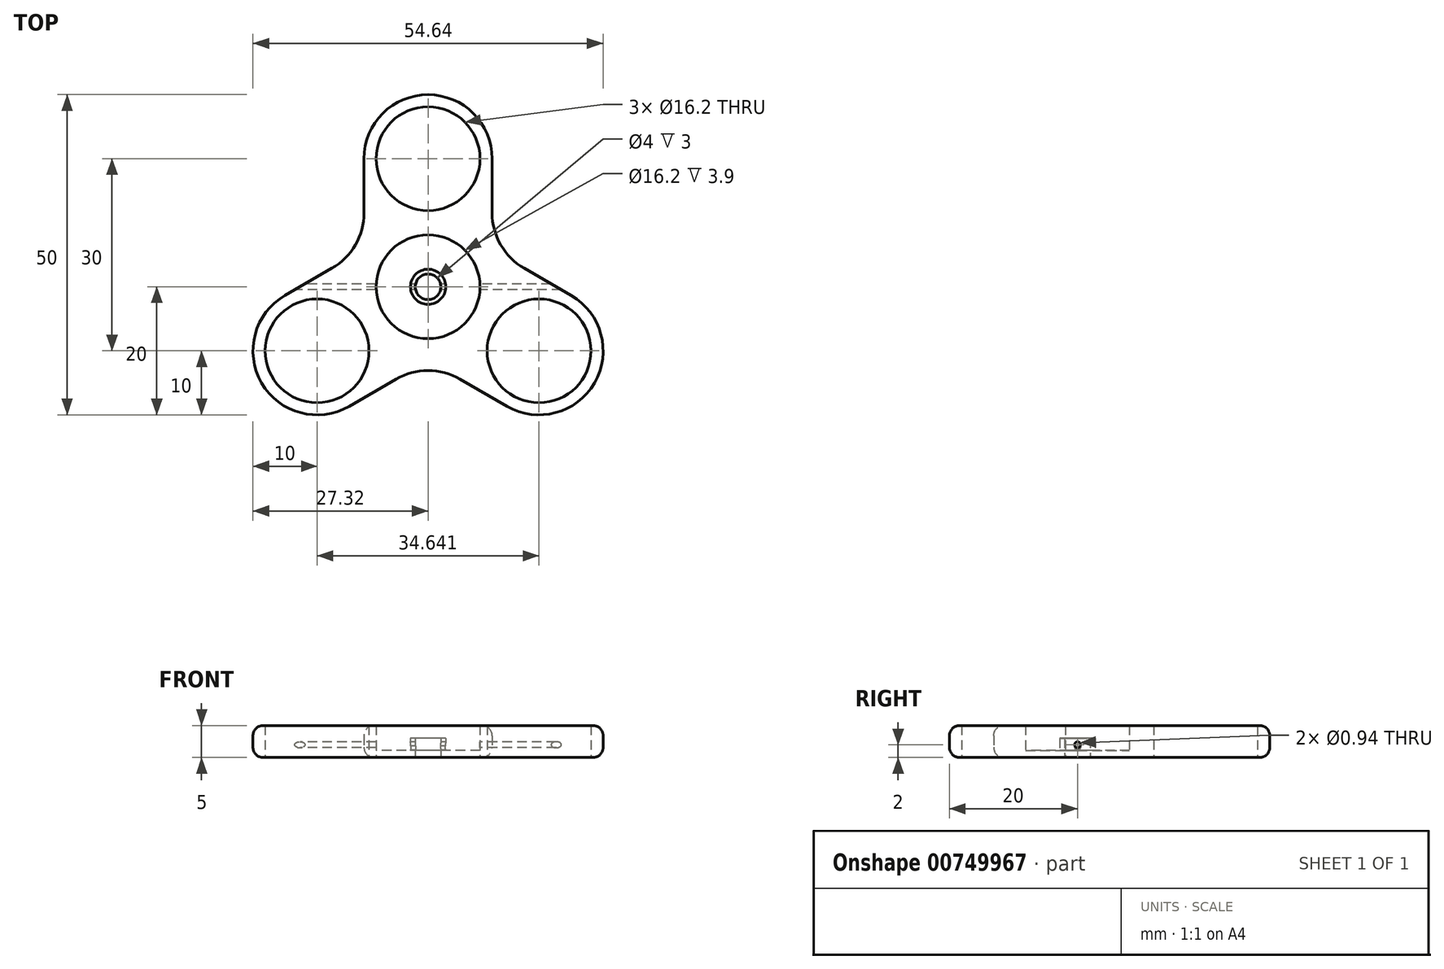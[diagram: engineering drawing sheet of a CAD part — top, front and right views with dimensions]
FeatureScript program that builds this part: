
annotation { "Feature Type Name" : "Feature", "Feature Type Description" : "" }
export const myFeature = defineFeature(function(context is Context, id is Id, definition is map)
    precondition{}
    {
        {
            var Q0;
            Q0=qCreatedBy(makeId("Top.planeOp"),FACE);
            var sketch = newSketch(context, id + "F0", { "sketchPlane" : qUnion([Q0])});
            skCircle(sketch, "E0", {"center": v(0, 0) * mm, "radius": 8.1 * mm});
            skCircle(sketch, "E1", {"center": v(0, 20) * mm, "radius": 8.1 * mm});
            skCircle(sketch, "E2.1.0", {"center": v(-17.32, -10) * mm, "radius": 8.1 * mm});
            skCircle(sketch, "E2.2.0", {"center": v(17.32, -10) * mm, "radius": 8.1 * mm});
            skLineSegment(sketch, "E3", {"start": v(-10, 20) * mm, "end": v(-10, 11.55) * mm});
            skLineSegment(sketch, "E4", {"start": v(10, 20) * mm, "end": v(10, 11.55) * mm});
            skArc(sketch, "E5", {"start": v(-10, 20) * mm, "mid": v(0, 30) * mm, "end": v(10, 20) * mm});
            skLineSegment(sketch, "E6.1.0", {"start": v(-12.32, -18.66) * mm, "end": v(-5, -14.43) * mm});
            skArc(sketch, "E6.1.1", {"start": v(-12.32, -18.66) * mm, "mid": v(-25.98, -15) * mm, "end": v(-22.32, -1.34) * mm});
            skLineSegment(sketch, "E6.1.2", {"start": v(-22.32, -1.34) * mm, "end": v(-15, 2.89) * mm});
            skLineSegment(sketch, "E6.2.0", {"start": v(22.32, -1.34) * mm, "end": v(15, 2.89) * mm});
            skArc(sketch, "E6.2.1", {"start": v(22.32, -1.34) * mm, "mid": v(25.98, -15) * mm, "end": v(12.32, -18.66) * mm});
            skLineSegment(sketch, "E6.2.2", {"start": v(12.32, -18.66) * mm, "end": v(5, -14.43) * mm});
            skPoint(sketch, "E7.orphan", {"position": v(-8.84, 6.44) * mm});
            skPoint(sketch, "E8.orphan", {"position": v(-10, 4.43) * mm});
            skPoint(sketch, "E9.orphan", {"position": v(8.84, 6.44) * mm});
            skPoint(sketch, "E10.orphan", {"position": v(10, 4.43) * mm});
            skPoint(sketch, "E11.orphan", {"position": v(1.16, -10.88) * mm});
            skPoint(sketch, "E12.orphan", {"position": v(-1.16, -10.88) * mm});
            skPoint(sketch, "E13.visualSharp", {"position": v(-10, 5.77) * mm});
            skArc(sketch, "E13.filletArc", {"start": v(-15, 2.89) * mm, "mid": v(-11.34, 6.55) * mm, "end": v(-10, 11.55) * mm});
            skPoint(sketch, "E14.visualSharp", {"position": v(10, 5.77) * mm});
            skArc(sketch, "E14.filletArc", {"start": v(10, 11.55) * mm, "mid": v(11.34, 6.55) * mm, "end": v(15, 2.89) * mm});
            skPoint(sketch, "E15.visualSharp", {"position": v(0, -11.55) * mm});
            skArc(sketch, "E15.filletArc", {"start": v(5, -14.43) * mm, "mid": v(0, -13.1) * mm, "end": v(-5, -14.43) * mm});
            skSolve(sketch);
        }
        {
            var Q0;
            Q0=makeQuery(id+"F0.imprint","IMPRINT",FACE,{"disambiguationData":[TD([[makeQuery(id+"F0.imprint","IMPRINT",EDGE,{"derivedFrom":sQuery(id+"F0.wireOp",EDGE,"E0")}),-1.0]])]});
            extrude(context, id + "F1", {"entities" : qUnion([Q0]), "depth" : 5 * mm, "offsetDistance" : 25 * mm});
        }
        {
            var Q0;
            Q0=makeQuery(id+"F1.opExtrude","SWEPT_FACE",FACE,{"disambiguationData":[OSD([sQuery(id+"F0.wireOp",EDGE,"E6.1.0")])]});
            fillet(context, id + "F2", {"entities" : qUnion([Q0]), "radius" : 1.6 * mm, "tangentPropagation" : true, "allowEdgeOverflow" : false});
        }
        {
            var Q0;
            Q0=qCreatedBy(makeId("Top.planeOp"),FACE);
            var sketch = newSketch(context, id + "F3", { "sketchPlane" : qUnion([Q0])});
            skCircle(sketch, "E16", {"center": v(0, 0) * mm, "radius": 8.5 * mm});
            skCircle(sketch, "E17", {"center": v(0, 0) * mm, "radius": 2 * mm});
            skCircle(sketch, "E18", {"center": v(0, 0) * mm, "radius": 2.75 * mm});
            skSolve(sketch);
        }
        {
            var Q0;
            Q0=makeQuery(id+"F3.imprint","IMPRINT",FACE,{"disambiguationData":[TD([[makeQuery(id+"F3.imprint","IMPRINT",EDGE,{"derivedFrom":sQuery(id+"F3.wireOp",EDGE,"E16")}),1.0]])]});
            var Q1;
            Q1=makeQuery(id+"F3.imprint","IMPRINT",FACE,{"disambiguationData":[TD([[makeQuery(id+"F3.imprint","IMPRINT",EDGE,{"derivedFrom":sQuery(id+"F3.wireOp",EDGE,"E17")}),-1.0]])]});
            extrude(context, id + "F4", {"entities" : qUnion([Q0, Q1]), "depth" : 1 * mm, "offsetDistance" : 25 * mm});
        }
        {
            var Q0;
            Q0=makeQuery(id+"F3.imprint","IMPRINT",FACE,{"disambiguationData":[TD([[makeQuery(id+"F3.imprint","IMPRINT",EDGE,{"derivedFrom":sQuery(id+"F3.wireOp",EDGE,"E17")}),-1.0]])]});
            extrude(context, id + "F5", {"entities" : qUnion([Q0]), "operationType" : NewBodyOperationType.ADD, "depth" : 3 * mm, "offsetDistance" : 25 * mm});
        }
        {
            var Q0;
            Q0=makeQuery(id+"F4.opExtrude","CAP_FACE",FACE,{"disambiguationData":[OSD([sQuery(id+"F3.wireOp",EDGE,"E16"),sQuery(id+"F3.wireOp",EDGE,"E17")])],"isStart":false});
            extrude(context, id + "F6", {"entities" : qUnion([Q0]), "operationType" : NewBodyOperationType.ADD, "depth" : 0.1 * mm, "offsetDistance" : 25 * mm});
        }
        {
            var Q0;
            Q0=qCreatedBy(makeId("Right.planeOp"),FACE);
            var sketch = newSketch(context, id + "F7", { "sketchPlane" : qUnion([Q0])});
            skPoint(sketch, "E19.center.orphan", {"position": v(0, 21.58) * mm});
            skPoint(sketch, "E20.start.orphan", {"position": v(0, 6.82) * mm});
            skLineSegment(sketch, "E21", {"start": v(0, 0) * mm, "end": v(0, 1.6) * mm});
            skCircle(sketch, "E22", {"center": v(0, 1.6) * mm, "radius": 0.47 * mm});
            skSolve(sketch);
        }
        {
            var Q0;
            Q0 = qSketchRegion(id + "F7", true);
            extrude(context, id + "F8", {"entities" : qUnion([Q0]), "operationType" : NewBodyOperationType.REMOVE, "depth" : 4 * mm, "offsetDistance" : 25 * mm, "hasSecondDirection" : true, "secondDirectionOppositeDirection" : true, "secondDirectionDepth" : 3 * mm});
        }
        {
            var Q0;
            Q0=qCreatedBy(makeId("Right.planeOp"),FACE);
            var sketch = newSketch(context, id + "F9", { "sketchPlane" : qUnion([Q0])});
            skLineSegment(sketch, "E23", {"start": v(0, 0) * mm, "end": v(0, 2) * mm});
            skCircle(sketch, "E24", {"center": v(0, 2) * mm, "radius": 0.47 * mm});
            skSolve(sketch);
        }
        {
            var Q0;
            Q0=makeQuery(id+"F9.imprint","IMPRINT",FACE,{"disambiguationData":[TD([[makeQuery(id+"F9.imprint","IMPRINT",EDGE,{"derivedFrom":sQuery(id+"F9.wireOp",EDGE,"E24")}),1.0]])]});
            extrude(context, id + "F10", {"entities" : qUnion([Q0]), "operationType" : NewBodyOperationType.REMOVE, "depth" : 25 * mm, "offsetDistance" : 25 * mm, "hasSecondDirection" : true, "secondDirectionOppositeDirection" : true, "secondDirectionDepth" : 25 * mm});
        }
    });
